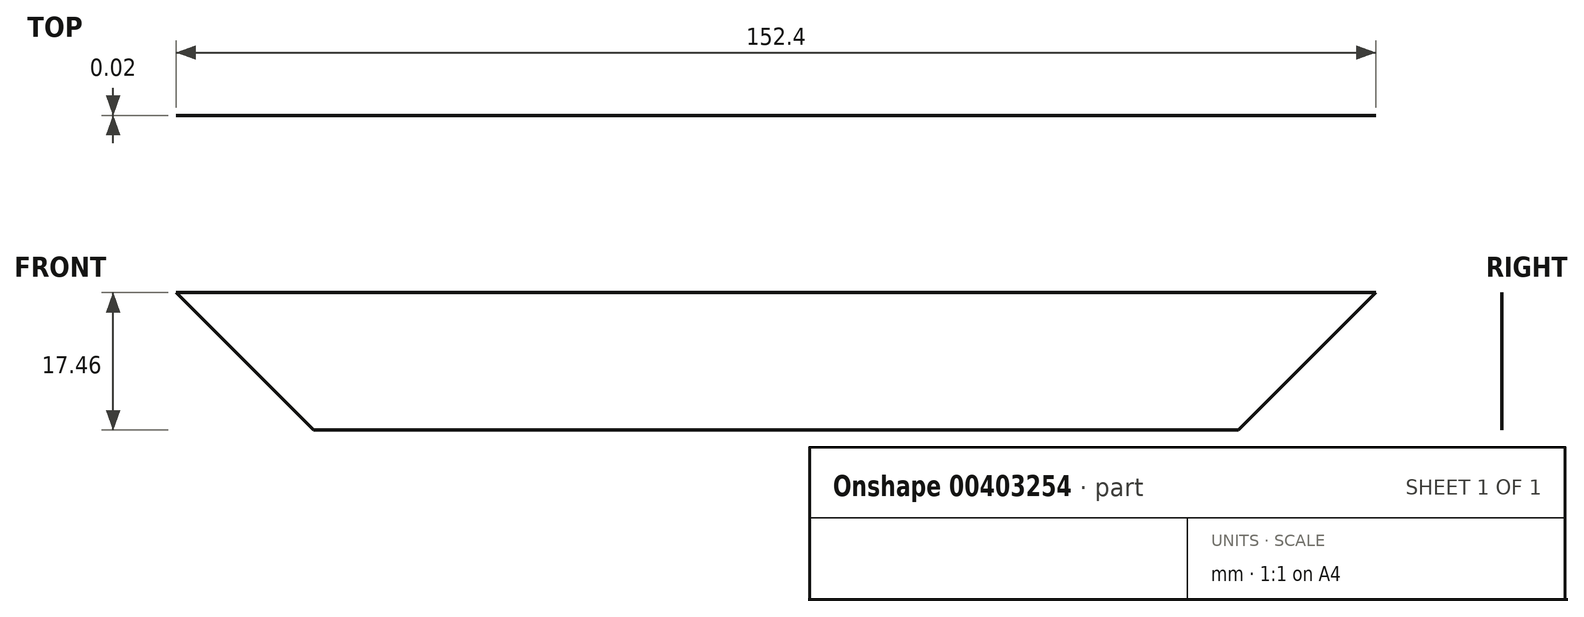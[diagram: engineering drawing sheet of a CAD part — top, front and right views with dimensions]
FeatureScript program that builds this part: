
annotation { "Feature Type Name" : "Feature", "Feature Type Description" : "" }
export const myFeature = defineFeature(function(context is Context, id is Id, definition is map)
    precondition{}
    {
        {
            var Q0;
            Q0=qCreatedBy(makeId("Front.planeOp"),FACE);
            var sketch = newSketch(context, id + "F0", { "sketchPlane" : qUnion([Q0])});
            skLineSegment(sketch, "E0.bottom", {"start": v(-76.2, 8.73) * mm, "end": v(76.2, 8.73) * mm});
            skLineSegment(sketch, "E0.top", {"start": v(-76.2, -8.73) * mm, "end": v(76.2, -8.73) * mm});
            skLineSegment(sketch, "E0.left", {"start": v(-76.2, 8.73) * mm, "end": v(-76.2, -8.73) * mm});
            skLineSegment(sketch, "E0.right", {"start": v(76.2, 8.73) * mm, "end": v(76.2, -8.73) * mm});
            skSolve(sketch);
        }
        {
            var Q0;
            Q0=makeQuery(id+"F0.imprint","IMPRINT",FACE,{"disambiguationData":[TD([[makeQuery(id+"F0.imprint","IMPRINT",EDGE,{"derivedFrom":sQuery(id+"F0.wireOp",EDGE,"E0.bottom")}),-1.0]])]});
            extrude(context, id + "F1", {"entities" : qUnion([Q0]), "endBound" : BoundingType.SYMMETRIC, "depth" : 11 / 406.4 * mm});
        }
        {
            var Q0;
            Q0=makeQuery(id+"F1.opExtrude","CAP_FACE",FACE,{"disambiguationData":[OSD([sQuery(id+"F0.wireOp",EDGE,"E0.bottom"),sQuery(id+"F0.wireOp",EDGE,"E0.top"),sQuery(id+"F0.wireOp",EDGE,"E0.left"),sQuery(id+"F0.wireOp",EDGE,"E0.right")])],"isStart":false});
            var sketch = newSketch(context, id + "F2", { "sketchPlane" : qUnion([Q0])});
            skLineSegment(sketch, "E1", {"start": v(-76.2, 8.73) * mm, "end": v(-58.74, -8.73) * mm});
            skLineSegment(sketch, "E2", {"start": v(-58.74, -8.73) * mm, "end": v(-76.2, -8.73) * mm});
            skLineSegment(sketch, "E3", {"start": v(-76.2, -8.73) * mm, "end": v(-76.2, 8.73) * mm});
            skLineSegment(sketch, "E4", {"start": v(76.2, 8.73) * mm, "end": v(58.74, -8.73) * mm});
            skLineSegment(sketch, "E5", {"start": v(58.74, -8.73) * mm, "end": v(76.2, -8.73) * mm});
            skLineSegment(sketch, "E6", {"start": v(76.2, -8.73) * mm, "end": v(76.2, 8.73) * mm});
            skSolve(sketch);
        }
        {
            var Q0;
            Q0=makeQuery(id+"F2.imprint","IMPRINT",FACE,{"disambiguationData":[TD([[makeQuery(id+"F2.imprint","IMPRINT",EDGE,{"derivedFrom":sQuery(id+"F2.wireOp",EDGE,"E1")}),-1.0]])]});
            extrude(context, id + "F3", {"entities" : qUnion([Q0]), "operationType" : NewBodyOperationType.REMOVE, "oppositeDirection" : true, "depth" : 11 / 406.4 * mm});
        }
        {
            var Q0;
            Q0=makeQuery(id+"F2.imprint","IMPRINT",FACE,{"disambiguationData":[TD([[makeQuery(id+"F2.imprint","IMPRINT",EDGE,{"derivedFrom":sQuery(id+"F2.wireOp",EDGE,"E4")}),1.0]])]});
            extrude(context, id + "F4", {"entities" : qUnion([Q0]), "operationType" : NewBodyOperationType.REMOVE, "oppositeDirection" : true, "depth" : 11 / 406.4 * mm});
        }
    });
